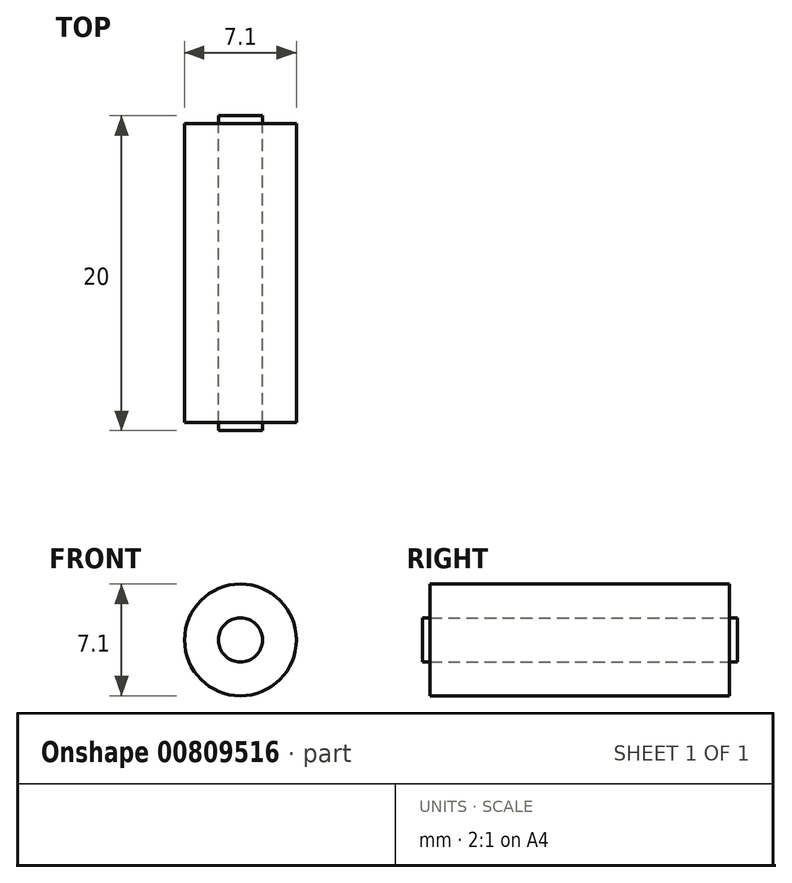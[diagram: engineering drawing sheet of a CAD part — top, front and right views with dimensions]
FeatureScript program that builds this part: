
annotation { "Feature Type Name" : "Feature", "Feature Type Description" : "" }
export const myFeature = defineFeature(function(context is Context, id is Id, definition is map)
    precondition{}
    {
        {
            var Q0;
            Q0=qCreatedBy(makeId("Front.planeOp"),FACE);
            var sketch = newSketch(context, id + "F0", { "sketchPlane" : qUnion([Q0])});
            skCircle(sketch, "E0", {"center": v(0, 0) * mm, "radius": 3.55 * mm});
            skSolve(sketch);
        }
        {
            var Q0;
            Q0=makeQuery(id+"F0.imprint","IMPRINT",FACE,{"disambiguationData":[TD([[makeQuery(id+"F0.imprint","IMPRINT",EDGE,{"derivedFrom":sQuery(id+"F0.wireOp",EDGE,"E0")}),1.0]])]});
            extrude(context, id + "F1", {"entities" : qUnion([Q0]), "endBound" : BoundingType.SYMMETRIC, "depth" : 19 * mm, "offsetDistance" : 25 * mm});
        }
        {
            var Q0;
            Q0=qCreatedBy(makeId("Front.planeOp"),FACE);
            var sketch = newSketch(context, id + "F2", { "sketchPlane" : qUnion([Q0])});
            skCircle(sketch, "E1", {"center": v(0, 0) * mm, "radius": 1.4 * mm});
            skSolve(sketch);
        }
        {
            var Q0;
            Q0 = qSketchRegion(id + "F2", true);
            extrude(context, id + "F3", {"entities" : qUnion([Q0]), "endBound" : BoundingType.SYMMETRIC, "depth" : 20 * mm, "offsetDistance" : 25 * mm});
        }
        {
            var Q0;
            Q0=qCreatedBy(makeId("Front.planeOp"),FACE);
            var sketch = newSketch(context, id + "F4", { "sketchPlane" : qUnion([Q0])});
            skLineSegment(sketch, "E2.bottom", {"start": v(0, 0) * mm, "end": v(10, 0) * mm});
            skLineSegment(sketch, "E2.top", {"start": v(0, 10) * mm, "end": v(10, 10) * mm});
            skLineSegment(sketch, "E2.left", {"start": v(0, 0) * mm, "end": v(0, 10) * mm});
            skLineSegment(sketch, "E2.right", {"start": v(10, 0) * mm, "end": v(10, 10) * mm});
            skSolve(sketch);
        }
        {
            var Q0;
            Q0=makeQuery(id+"F4.imprint","IMPRINT",FACE,{"disambiguationData":[TD([[makeQuery(id+"F4.imprint","IMPRINT",EDGE,{"derivedFrom":sQuery(id+"F4.wireOp",EDGE,"E2.bottom")}),1.0]])]});
            extrude(context, id + "F5", {"entities" : qUnion([Q0]), "depth" : 10 * mm, "offsetDistance" : 25 * mm});
        }
        {
            var Q0;
            Q0=makeQuery(id+"F5.opExtrude","SWEPT_BODY",BODY,{"disambiguationData":[OSD([sQuery(id+"F4.wireOp",EDGE,"E2.bottom"),sQuery(id+"F4.wireOp",EDGE,"E2.top"),sQuery(id+"F4.wireOp",EDGE,"E2.left"),sQuery(id+"F4.wireOp",EDGE,"E2.right")])]});
            deleteBodies(context, id + "F6", {"entities" : qUnion([Q0])});
        }
    });
